# Revit family: Lighting - Alva Tess Slotted Wall Sconce
name_source: partatom
category: Lighting Fixtures
revit_build: Autodesk Revit 2017 (Build: 20190508_0315(x64)
units: mm (PartAtom-declared; Revit-internal decimal feet)

## family parameters
Cut with Voids When Loaded = No
Host = Face
Light Source = Yes
Part Type = Normal
Room Calculation Point = No
Round Connector Dimension = Use Diameter
Shared = No

## types (18) — shared parameters
Color Filter = 16777215
Default Elevation = 4' - 0"
Description = ARCHITECTURAL SCALE, WET-LISTED EXTERIOR WALL SCONCE
Dimming Lamp Color Temperature Shift = <None>
Emit from Line Length = 3' - 7"
Height = 3' - 9"
Lamp = LED
Lens = ALVA Lens
Light Source Symbol Size = 1' - 0"
Manufacturer = ALVA LIGHTING
Type Comments = IP66 RATED, 120-277V INPUT, 0-10V DIMMING, 10 YEAR LIMITED WARRANTY, 85 CRI
URL = https://www.alvalight.com

## per-type parameters (varying)
| type | Apparent Load | Metal | Model |
| 30" 3000k ESN | 23 VA | ALVA Enviro Satin Nickel | TESS 30 3000K ESN |
| 30" 3000k GR | 23 VA | ALVA Graphite | TESS 30 3000K GR |
| 30" 3000k EOB | 23 VA | ALVA Enviro Oil-Rubbed Bronze | TESS 30 3000K EOB |
| 30" 3000k BLK | 23 VA | ALVA Matt Black | TESS 30 3000K BLK |
| 30" 3000k WHT | 23 VA | ALVA Matt White | TESS 30 3000K WHT |
| 30" 3000k DBT | 23 VA | ALVA Dark Bronze Textured | TESS 30 3000K DBT |
| 45" 3000k DBT | 29 VA | ALVA Dark Bronze Textured | TESS 45 3000K DBT |
| 45" 3000k EOB | 29 VA | ALVA Enviro Oil-Rubbed Bronze | TESS 45 3000K EOB |
| 45" 3000k WHT | 29 VA | ALVA Matt White | TESS 45 3000K WHT |
| 45" 3000k BLK | 29 VA | ALVA Matt Black | TESS 45 3000K BLK |
| 45" 3000k ESN | 29 VA | ALVA Enviro Satin Nickel | TESS 45 3000K ESN |
| 45" 3000k GR | 29 VA | ALVA Graphite | TESS 45 3000K GR |
| 60" 3000k GR | 37 VA | ALVA Graphite | TESS 60 3000K GR |
| 60" 3000k WHT | 37 VA | ALVA Matt White | TESS 60 3000K WHT |
| 60" 3000k BLK | 37 VA | ALVA Matt Black | TESS 60 3000K BLK |
| 60" 3000k EOB | 37 VA | ALVA Enviro Oil-Rubbed Bronze | TESS 60 3000K EOB |
| 60" 3000k DBT | 37 VA | ALVA Dark Bronze Textured | TESS 60 3000K DBT |
| 60" 3000k ESN | 37 VA | ALVA Enviro Satin Nickel | TESS 60 3000K ESN |

## geometry (parser evidence)
native form markers: Sweep x1
no freeform markers — native parametric forms only
